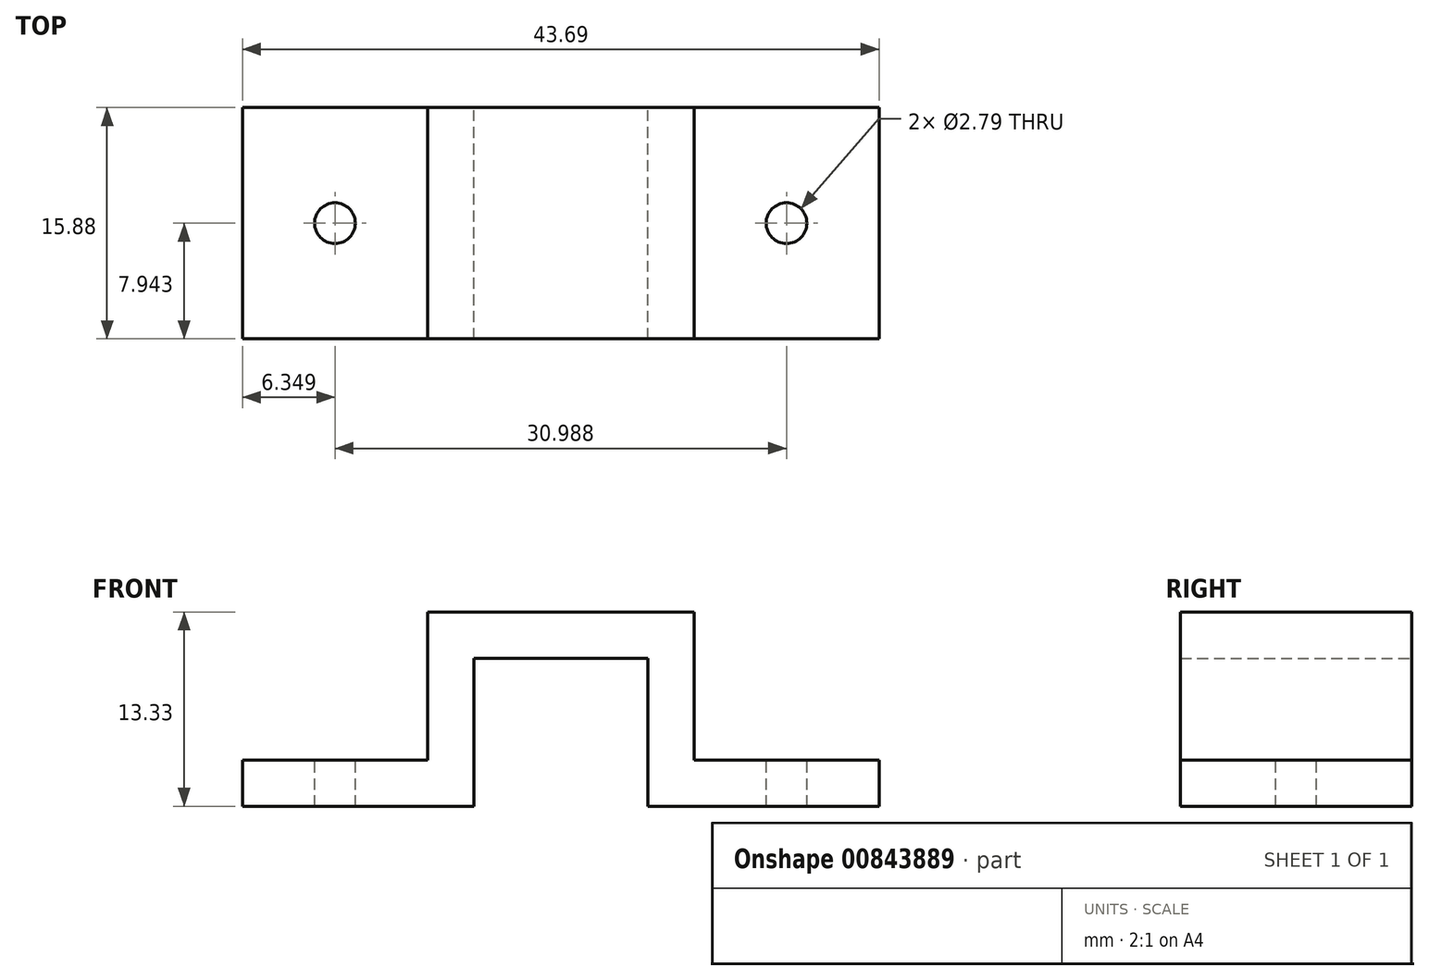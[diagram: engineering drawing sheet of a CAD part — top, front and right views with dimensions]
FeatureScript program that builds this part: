
annotation { "Feature Type Name" : "Feature", "Feature Type Description" : "" }
export const myFeature = defineFeature(function(context is Context, id is Id, definition is map)
    precondition{}
    {
        {
            var Q0;
            Q0=qCreatedBy(makeId("Front.planeOp"),FACE);
            var sketch = newSketch(context, id + "F0", { "sketchPlane" : qUnion([Q0])});
            skLineSegment(sketch, "E0.top", {"start": v(0.7, 1.43) * mm, "end": v(12.64, 1.43) * mm});
            skLineSegment(sketch, "E0.left", {"start": v(-2.47, 4.6) * mm, "end": v(-2.47, 0) * mm});
            skLineSegment(sketch, "E1.top", {"start": v(-2.47, -8.73) * mm, "end": v(0.7, -8.73) * mm});
            skLineSegment(sketch, "E1.left", {"start": v(-2.47, 0) * mm, "end": v(-2.47, -5.56) * mm});
            skLineSegment(sketch, "E1.right", {"start": v(0.7, 1.43) * mm, "end": v(0.7, -8.73) * mm});
            skLineSegment(sketch, "E2.bottom", {"start": v(0.7, -8.73) * mm, "end": v(-15.17, -8.73) * mm});
            skLineSegment(sketch, "E2.top", {"start": v(-2.47, -5.56) * mm, "end": v(-15.17, -5.56) * mm});
            skLineSegment(sketch, "E2.left", {"start": v(0.7, -8.73) * mm, "end": v(0.7, -5.56) * mm});
            skLineSegment(sketch, "E2.right", {"start": v(-15.17, -8.73) * mm, "end": v(-15.17, -5.56) * mm});
            skLineSegment(sketch, "E3.left", {"start": v(15.82, 4.6) * mm, "end": v(15.82, -5.56) * mm});
            skLineSegment(sketch, "E3.right", {"start": v(12.64, 1.43) * mm, "end": v(12.64, -8.73) * mm});
            skLineSegment(sketch, "E4.left", {"start": v(12.64, -8.73) * mm, "end": v(12.64, -5.56) * mm});
            skLineSegment(sketch, "E5", {"start": v(-2.47, 4.6) * mm, "end": v(15.82, 4.6) * mm});
            skLineSegment(sketch, "E6", {"start": v(15.82, -5.56) * mm, "end": v(28.52, -5.56) * mm});
            skLineSegment(sketch, "E7", {"start": v(28.52, -5.56) * mm, "end": v(28.52, -8.73) * mm});
            skLineSegment(sketch, "E8", {"start": v(28.52, -8.73) * mm, "end": v(12.64, -8.73) * mm});
            skSolve(sketch);
        }
        {
            var Q0;
            Q0=makeQuery(id+"F0.imprint","IMPRINT",FACE,{"disambiguationData":[TD([[makeQuery(id+"F0.imprint","IMPRINT",EDGE,{"derivedFrom":sQuery(id+"F0.wireOp",EDGE,"E0.top")}),1.0]])]});
            extrude(context, id + "F1", {"entities" : qUnion([Q0]), "depth" : 15.88 * mm, "offsetDistance" : 25.4 * mm});
        }
        {
            var Q0;
            Q0=makeQuery(id+"F1.opExtrude","SWEPT_FACE",FACE,{"disambiguationData":[OSD([sQuery(id+"F0.wireOp",EDGE,"E2.top")])]});
            var sketch = newSketch(context, id + "F2", { "sketchPlane" : qUnion([Q0])});
            skCircle(sketch, "E9", {"center": v(-8.82, -7.94) * mm, "radius": 1.4 * mm});
            skCircle(sketch, "E10", {"center": v(22.17, -7.94) * mm, "radius": 1.4 * mm});
            skSolve(sketch);
        }
        {
            var Q0;
            Q0=makeQuery(id+"F2.imprint","IMPRINT",FACE,{"disambiguationData":[TD([[makeQuery(id+"F2.imprint","IMPRINT",EDGE,{"derivedFrom":sQuery(id+"F2.wireOp",EDGE,"E9")}),1.0]])]});
            var Q1;
            Q1=makeQuery(id+"F2.imprint","IMPRINT",FACE,{"disambiguationData":[TD([[makeQuery(id+"F2.imprint","IMPRINT",EDGE,{"derivedFrom":sQuery(id+"F2.wireOp",EDGE,"E10")}),1.0]])]});
            extrude(context, id + "F3", {"entities" : qUnion([Q0, Q1]), "operationType" : NewBodyOperationType.REMOVE, "oppositeDirection" : true, "depth" : 25.4 * mm, "offsetDistance" : 25.4 * mm});
        }
    });
